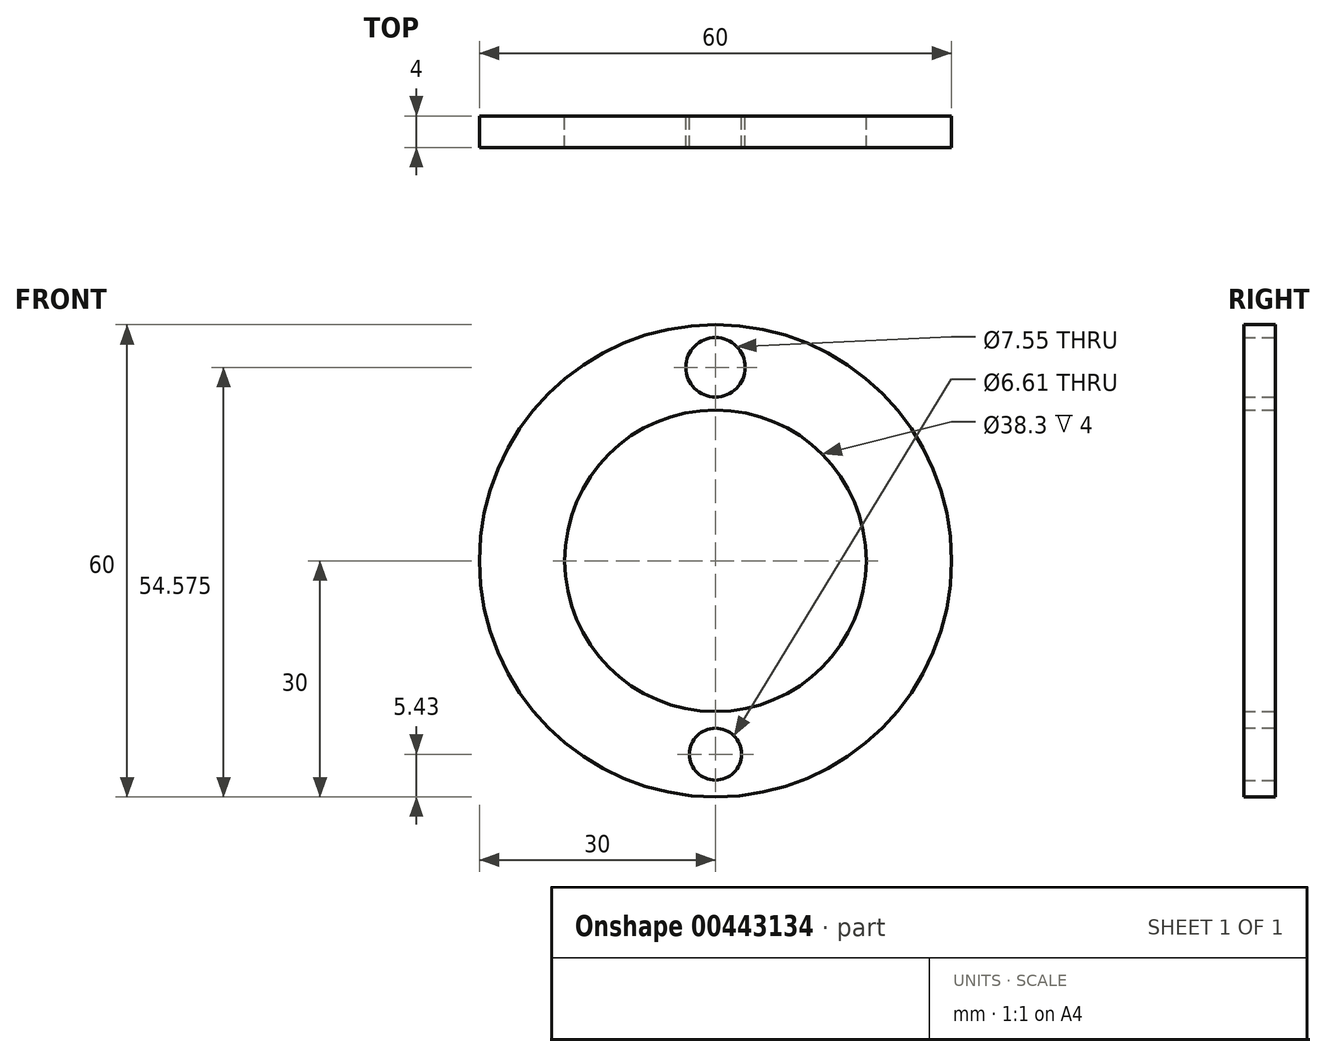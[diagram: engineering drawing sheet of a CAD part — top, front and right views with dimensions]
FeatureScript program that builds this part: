
annotation { "Feature Type Name" : "Feature", "Feature Type Description" : "" }
export const myFeature = defineFeature(function(context is Context, id is Id, definition is map)
    precondition{}
    {
        {
            var Q0;
            Q0=qCreatedBy(makeId("Front.planeOp"),FACE);
            var sketch = newSketch(context, id + "F0", { "sketchPlane" : qUnion([Q0])});
            skCircle(sketch, "E0", {"center": v(0, 0) * mm, "radius": 30 * mm});
            skCircle(sketch, "E1", {"center": v(0, 0) * mm, "radius": 19.15 * mm});
            skLineSegment(sketch, "E2", {"start": v(0, 19.15) * mm, "end": v(0, 30) * mm});
            skLineSegment(sketch, "E3", {"start": v(0, 19.15) * mm, "end": v(0, 24.57) * mm});
            skCircle(sketch, "E4", {"center": v(0, 24.57) * mm, "radius": 3.78 * mm});
            skLineSegment(sketch, "E5", {"start": v(0, -19.15) * mm, "end": v(0, -24.57) * mm});
            skCircle(sketch, "E6", {"center": v(0, -24.57) * mm, "radius": 3.3 * mm});
            skSolve(sketch);
        }
        {
            var Q0;
            Q0=makeQuery(id+"F0.imprint","IMPRINT",FACE,{"disambiguationData":[TD([[makeQuery(id+"F0.imprint","IMPRINT",EDGE,{"derivedFrom":sQuery(id+"F0.wireOp",EDGE,"E0")}),1.0]])]});
            extrude(context, id + "F1", {"entities" : qUnion([Q0]), "depth" : 4 * mm});
        }
    });
